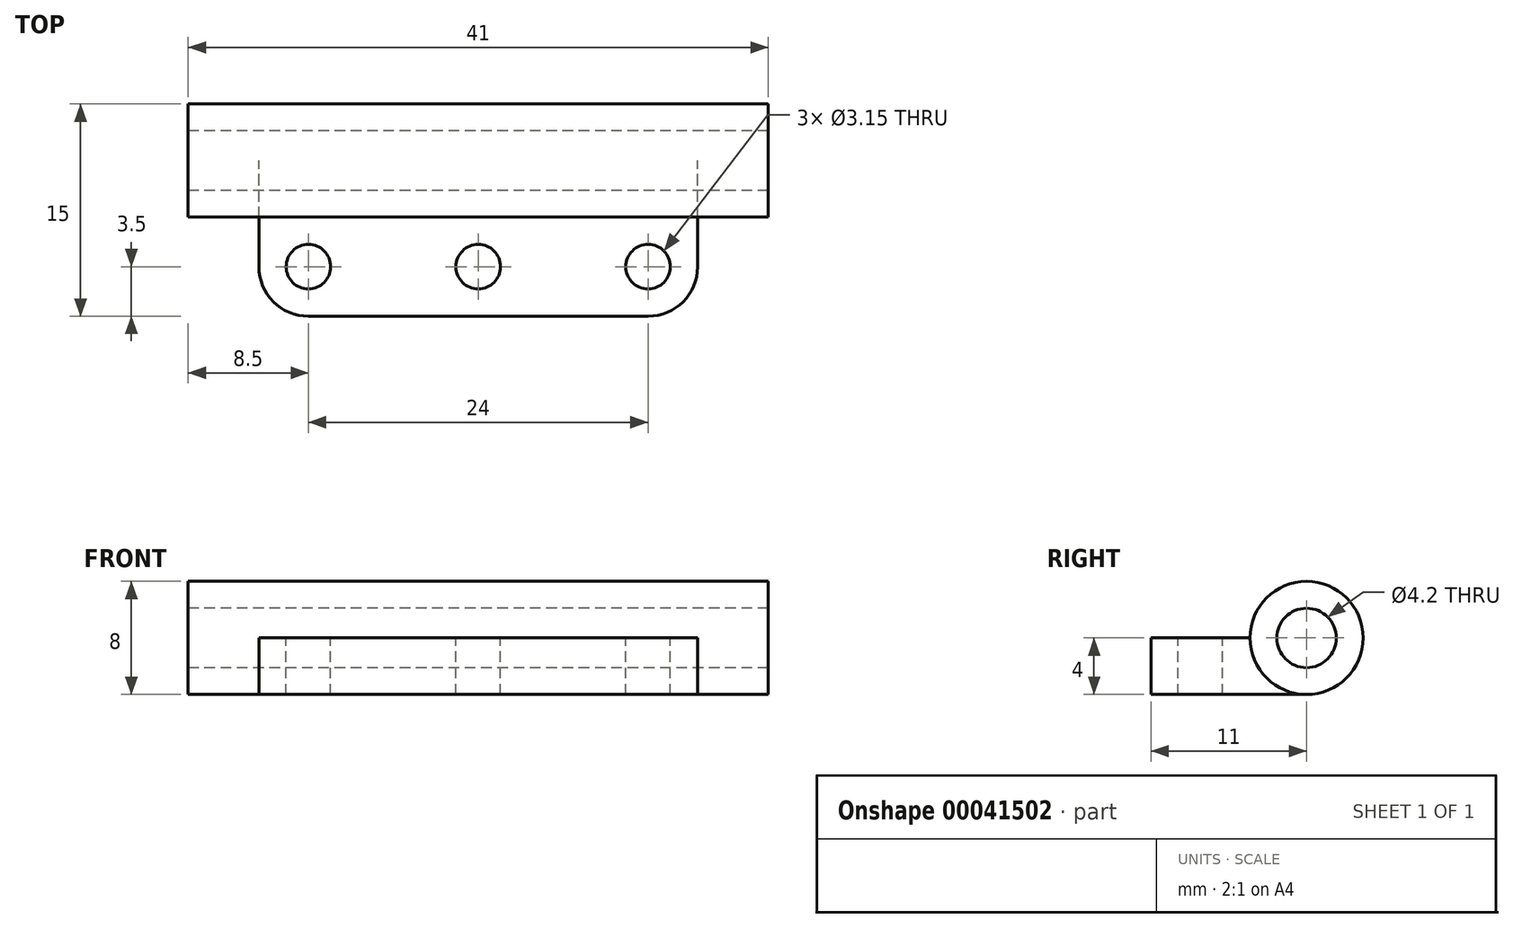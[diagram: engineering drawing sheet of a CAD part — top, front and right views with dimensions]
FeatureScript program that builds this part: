
annotation { "Feature Type Name" : "Feature", "Feature Type Description" : "" }
export const myFeature = defineFeature(function(context is Context, id is Id, definition is map)
    precondition{}
    {
        {
            var Q0;
            Q0=qCreatedBy(makeId("Right.planeOp"),FACE);
            var sketch = newSketch(context, id + "F0", { "sketchPlane" : qUnion([Q0])});
            skCircle(sketch, "E0", {"center": v(0, 0) * mm, "radius": 2.1 * mm});
            skLineSegment(sketch, "E1.bottom", {"start": v(0, 4) * mm, "end": v(0, 4) * mm});
            skLineSegment(sketch, "E1.top", {"start": v(-4, -4) * mm, "end": v(0, -4) * mm});
            skLineSegment(sketch, "E1.left", {"start": v(-4, 0) * mm, "end": v(-4, 0) * mm});
            skLineSegment(sketch, "E1.right", {"start": v(4, 0) * mm, "end": v(4, 0) * mm});
            skLineSegment(sketch, "E2", {"start": v(-4, 0) * mm, "end": v(-11, 0) * mm});
            skLineSegment(sketch, "E3", {"start": v(-11, 0) * mm, "end": v(-11, -4) * mm});
            skLineSegment(sketch, "E4", {"start": v(-11, -4) * mm, "end": v(-4, -4) * mm});
            skLineSegment(sketch, "E5", {"start": v(-4, 0) * mm, "end": v(4, 0) * mm, "construction": true});
            skPoint(sketch, "E6.visualSharp", {"position": v(-4, 4) * mm});
            skArc(sketch, "E6.filletArc", {"start": v(0, 4) * mm, "mid": v(-2.83, 2.83) * mm, "end": v(-4, 0) * mm});
            skPoint(sketch, "E7.visualSharp", {"position": v(4, 4) * mm});
            skArc(sketch, "E7.filletArc", {"start": v(4, 0) * mm, "mid": v(2.83, 2.83) * mm, "end": v(0, 4) * mm});
            skPoint(sketch, "E8.visualSharp", {"position": v(4, -4) * mm});
            skArc(sketch, "E8.filletArc", {"start": v(0, -4) * mm, "mid": v(2.83, -2.83) * mm, "end": v(4, 0) * mm});
            skSolve(sketch);
        }
        {
            var Q0;
            Q0 = qSketchRegion(id + "F0", true);
            extrude(context, id + "F1", {"entities" : qUnion([Q0]), "depth" : 31 * mm});
        }
        {
            var Q0;
            Q0=makeQuery(id+"F1.opExtrude","CAP_EDGE",EDGE,{"disambiguationData":[OSD([sQuery(id+"F0.wireOp",EDGE,"E3")])],"isStart":false});
            var Q1;
            Q1=makeQuery(id+"F1.opExtrude","CAP_EDGE",EDGE,{"disambiguationData":[OSD([sQuery(id+"F0.wireOp",EDGE,"E3")])],"isStart":true});
            fillet(context, id + "F2", {"entities" : qUnion([Q0, Q1]), "radius" : 3.5 * mm, "tangentPropagation" : true, "allowEdgeOverflow" : false});
        }
        {
            var Q0;
            Q0=makeQuery(id+"F1.opExtrude","SWEPT_FACE",FACE,{"disambiguationData":[OSD([sQuery(id+"F0.wireOp",EDGE,"E2")])]});
            var sketch = newSketch(context, id + "F3", { "sketchPlane" : qUnion([Q0])});
            skPoint(sketch, "E9", {"position": v(27.5, -7.5) * mm});
            skPoint(sketch, "E10", {"position": v(3.5, -7.5) * mm});
            skLineSegment(sketch, "E11", {"start": v(3.5, -7.5) * mm, "end": v(27.5, -7.5) * mm, "construction": true});
            skPoint(sketch, "E12", {"position": v(15.5, -7.5) * mm});
            skSolve(sketch);
        }
        {
            var Q0;
            Q0=sQuery(id+"F3.wireOp",VERTEX,"E10");
            var Q1;
            Q1=sQuery(id+"F3.wireOp",VERTEX,"E9");
            var Q2;
            Q2=sQuery(id+"F3.wireOp",VERTEX,"E12");
            var Q3;
            Q3=makeQuery(id+"F1.opExtrude","SWEPT_BODY",BODY,{"disambiguationData":[OSD([sQuery(id+"F0.wireOp",EDGE,"E0"),sQuery(id+"F0.wireOp",EDGE,"E1.top"),sQuery(id+"F0.wireOp",EDGE,"E2"),sQuery(id+"F0.wireOp",EDGE,"E3"),sQuery(id+"F0.wireOp",EDGE,"E4"),sQuery(id+"F0.wireOp",EDGE,"E6.filletArc"),sQuery(id+"F0.wireOp",EDGE,"E7.filletArc"),sQuery(id+"F0.wireOp",EDGE,"E8.filletArc")])]});
            hole(context, id + "F4", {"style" : HoleStyle.SIMPLE, "holeDiameter" : 3.15 * mm, "endStyle" : HoleEndStyle.THROUGH, "locations" : qUnion([Q0, Q1, Q2]), "scope" : qUnion([Q3])});
        }
        {
            var Q0;
            Q0=makeQuery(id+"F1.opExtrude","CAP_FACE",FACE,{"disambiguationData":[OSD([sQuery(id+"F0.wireOp",EDGE,"E0"),sQuery(id+"F0.wireOp",EDGE,"E1.top"),sQuery(id+"F0.wireOp",EDGE,"E2"),sQuery(id+"F0.wireOp",EDGE,"E3"),sQuery(id+"F0.wireOp",EDGE,"E4"),sQuery(id+"F0.wireOp",EDGE,"E6.filletArc"),sQuery(id+"F0.wireOp",EDGE,"E7.filletArc"),sQuery(id+"F0.wireOp",EDGE,"E8.filletArc")])],"isStart":false});
            var sketch = newSketch(context, id + "F5", { "sketchPlane" : qUnion([Q0])});
            skCircle(sketch, "E13", {"center": v(0, 0) * mm, "radius": 4 * mm});
            skCircle(sketch, "E14", {"center": v(0, 0) * mm, "radius": 2.1 * mm});
            skSolve(sketch);
        }
        {
            var Q0;
            Q0=makeQuery(id+"F5.imprint","IMPRINT",FACE,{"disambiguationData":[TD([[makeQuery(id+"F5.imprint","IMPRINT",EDGE,{"derivedFrom":sQuery(id+"F5.wireOp",EDGE,"E14")}),-1.0]])]});
            extrude(context, id + "F6", {"entities" : qUnion([Q0]), "operationType" : NewBodyOperationType.ADD, "depth" : 5 * mm});
        }
        {
            var Q0;
            Q0=makeQuery(id+"F1.opExtrude","CAP_FACE",FACE,{"disambiguationData":[OSD([sQuery(id+"F0.wireOp",EDGE,"E0"),sQuery(id+"F0.wireOp",EDGE,"E1.top"),sQuery(id+"F0.wireOp",EDGE,"E2"),sQuery(id+"F0.wireOp",EDGE,"E3"),sQuery(id+"F0.wireOp",EDGE,"E4"),sQuery(id+"F0.wireOp",EDGE,"E6.filletArc"),sQuery(id+"F0.wireOp",EDGE,"E7.filletArc"),sQuery(id+"F0.wireOp",EDGE,"E8.filletArc")])],"isStart":true});
            var sketch = newSketch(context, id + "F7", { "sketchPlane" : qUnion([Q0])});
            skCircle(sketch, "E15", {"center": v(0, 0) * mm, "radius": 4 * mm});
            skCircle(sketch, "E16", {"center": v(0, 0) * mm, "radius": 2.1 * mm});
            skSolve(sketch);
        }
        {
            var Q0;
            {var subQ0=sQuery(id+"F7.wireOp",EDGE,"E15");Q0=makeQuery(id+"F7.imprint","IMPRINT",FACE,{"disambiguationData":[TD([[makeQuery(id+"F7.imprint","IMPRINT",EDGE,{"disambiguationData":[OD(0.0)],"derivedFrom":subQ0}),-1.0]])]});}
            extrude(context, id + "F8", {"entities" : qUnion([Q0]), "operationType" : NewBodyOperationType.ADD, "depth" : 5 * mm});
        }
    });
